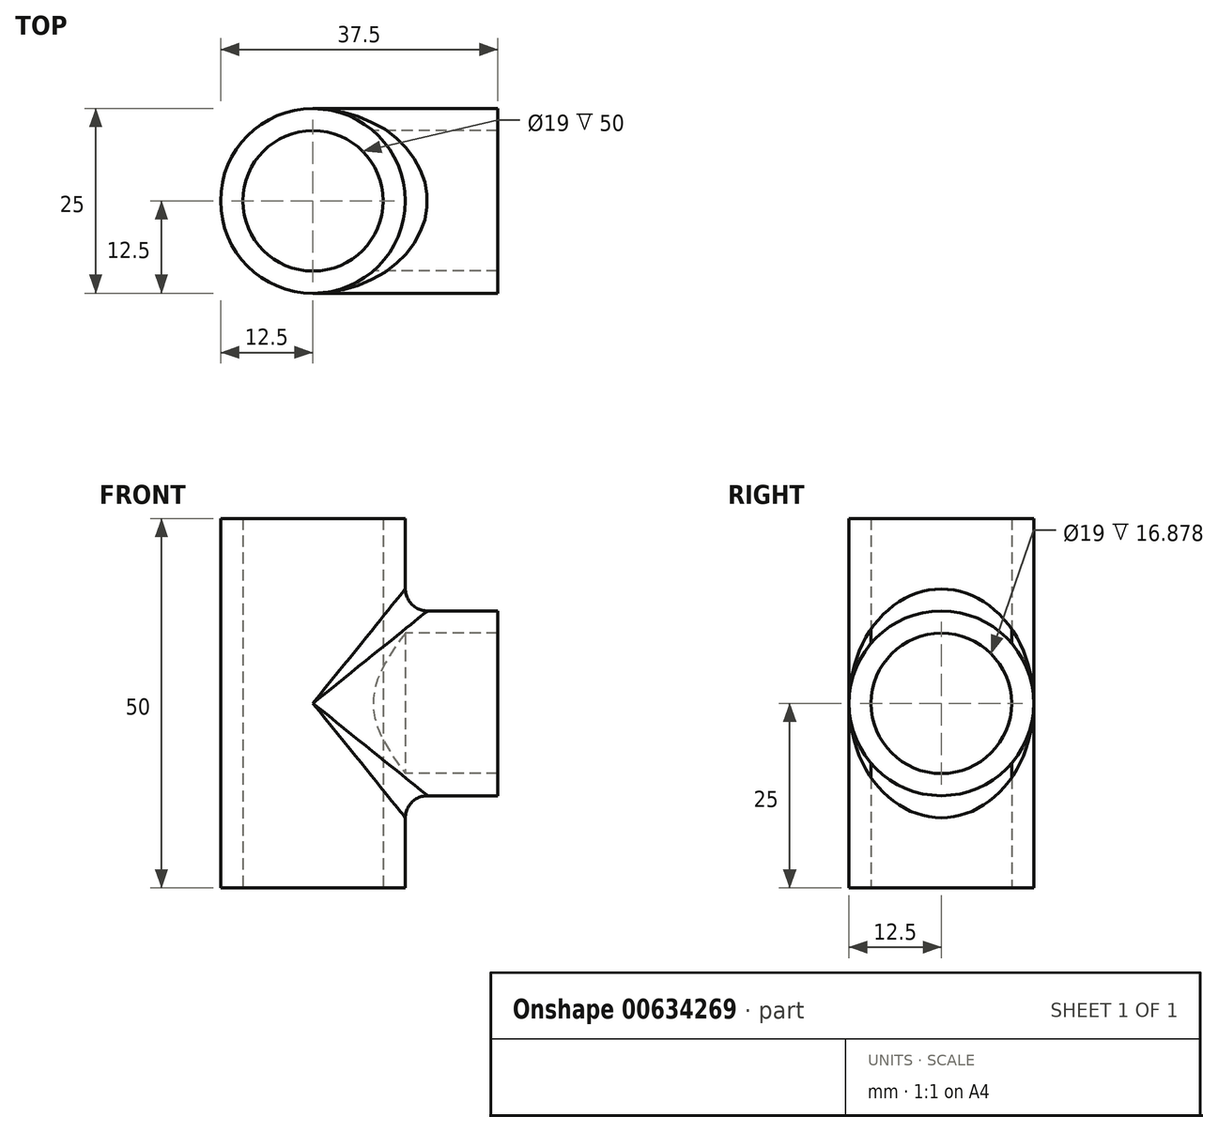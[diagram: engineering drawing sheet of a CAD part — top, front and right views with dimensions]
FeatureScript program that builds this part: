
annotation { "Feature Type Name" : "Feature", "Feature Type Description" : "" }
export const myFeature = defineFeature(function(context is Context, id is Id, definition is map)
    precondition{}
    {
        {
            var Q0;
            Q0=qCreatedBy(makeId("Top.planeOp"),FACE);
            var sketch = newSketch(context, id + "F0", { "sketchPlane" : qUnion([Q0])});
            skCircle(sketch, "E0", {"center": v(0, 0) * mm, "radius": 12.5 * mm});
            skCircle(sketch, "E1", {"center": v(0, 0) * mm, "radius": 9.5 * mm});
            skSolve(sketch);
        }
        {
            var Q0;
            Q0=qSketchRegion(id+"F0",true);
            extrude(context, id + "F1", {"entities" : qUnion([Q0]), "depth" : 50 * mm, "offsetDistance" : 25 * mm});
        }
        {
            var Q0;
            Q0=qCreatedBy(makeId("Right.planeOp"),FACE);
            var sketch = newSketch(context, id + "F2", { "sketchPlane" : qUnion([Q0])});
            skLineSegment(sketch, "E2", {"start": v(0, 0) * mm, "end": v(0, 50) * mm});
            skCircle(sketch, "E3", {"center": v(0, 25) * mm, "radius": 12.5 * mm});
            skCircle(sketch, "E4", {"center": v(0, 25) * mm, "radius": 9.5 * mm});
            skSolve(sketch);
        }
        {
            var Q0;
            Q0=qSketchRegion(id+"F2",true);
            extrude(context, id + "F3", {"entities" : qUnion([Q0]), "operationType" : NewBodyOperationType.ADD, "depth" : 25 * mm, "offsetDistance" : 25 * mm});
        }
        {
            var Q0;
            Q0=makeQuery(id+"F3.boolean.opBoolean","INTERSECT",EDGE,{"disambiguationData":[OD(1.0)],"derivedFrom":[makeQuery(id+"F1.opExtrude","SWEPT_FACE",FACE,{"disambiguationData":[OSD([sQuery(id+"F0.wireOp",EDGE,"E0")])]}),makeQuery(id+"F3.opExtrude","SWEPT_FACE",FACE,{"disambiguationData":[OSD([sQuery(id+"F2.wireOp",EDGE,"E3")])]})]});
            var Q1;
            Q1=makeQuery(id+"F3.boolean.opBoolean","INTERSECT",EDGE,{"disambiguationData":[OD(0.0)],"derivedFrom":[makeQuery(id+"F1.opExtrude","SWEPT_FACE",FACE,{"disambiguationData":[OSD([sQuery(id+"F0.wireOp",EDGE,"E0")])]}),makeQuery(id+"F3.opExtrude","SWEPT_FACE",FACE,{"disambiguationData":[OSD([sQuery(id+"F2.wireOp",EDGE,"E3")])]})]});
            fillet(context, id + "F4", {"entities" : qUnion([Q0, Q1]), "radius" : 3 * mm, "tangentPropagation" : true, "allowEdgeOverflow" : false});
        }
        {
            var Q0;
            Q0=qCreatedBy(makeId("Top.planeOp"),FACE);
            var sketch = newSketch(context, id + "F5", { "sketchPlane" : qUnion([Q0])});
            skCircle(sketch, "E5.0", {"center": v(0, 0) * mm, "radius": 9.5 * mm});
            skSolve(sketch);
        }
        {
            var Q0;
            Q0=qSketchRegion(id+"F5",true);
            extrude(context, id + "F6", {"entities" : qUnion([Q0]), "operationType" : NewBodyOperationType.REMOVE, "depth" : 50 * mm, "offsetDistance" : 25 * mm});
        }
    });
